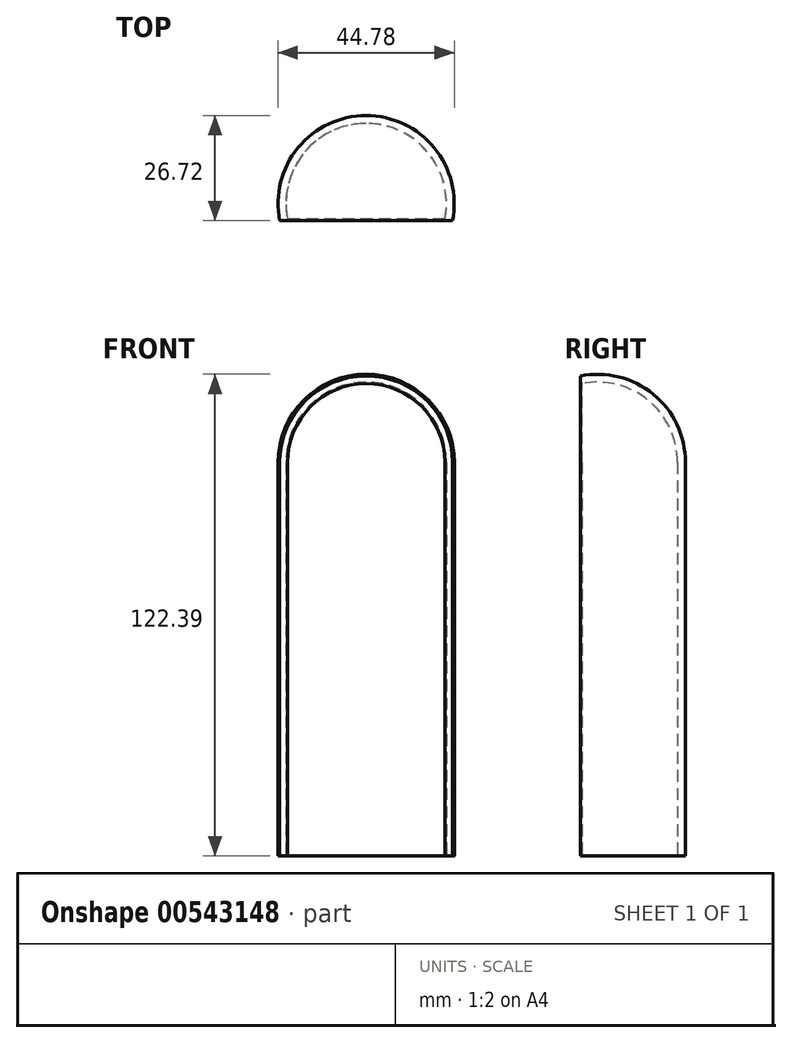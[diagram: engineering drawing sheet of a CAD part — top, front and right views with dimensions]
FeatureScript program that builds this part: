
annotation { "Feature Type Name" : "Feature", "Feature Type Description" : "" }
export const myFeature = defineFeature(function(context is Context, id is Id, definition is map)
    precondition{}
    {
        {
            var Q0;
            Q0=qCreatedBy(makeId("Top.planeOp"),FACE);
            var sketch = newSketch(context, id + "F0", { "sketchPlane" : qUnion([Q0])});
            skArc(sketch, "E0", {"start": v(40, 0) * mm, "mid": v(20, 24.33) * mm, "end": v(0, 0) * mm});
            skArc(sketch, "E1.0", {"start": v(41.96, -0.39) * mm, "mid": v(20, 26.33) * mm, "end": v(-1.96, -0.39) * mm});
            skLineSegment(sketch, "E2", {"start": v(-1.96, -0.39) * mm, "end": v(0, 0) * mm});
            skLineSegment(sketch, "E3", {"start": v(40, 0) * mm, "end": v(41.96, -0.39) * mm});
            skSolve(sketch);
        }
        {
            var Q0;
            Q0=makeQuery(id+"F0.imprint","IMPRINT",FACE,{"disambiguationData":[TD([[makeQuery(id+"F0.imprint","IMPRINT",EDGE,{"derivedFrom":sQuery(id+"F0.wireOp",EDGE,"E0")}),-1.0]])]});
            extrude(context, id + "F1", {"entities" : qUnion([Q0]), "depth" : 100 * mm, "offsetDistance" : 25.4 * mm});
        }
        {
            var Q0;
            Q0=makeQuery(id+"F1.opExtrude","CAP_FACE",FACE,{"disambiguationData":[OSD([sQuery(id+"F0.wireOp",EDGE,"E0"),sQuery(id+"F0.wireOp",EDGE,"E1.0"),sQuery(id+"F0.wireOp",EDGE,"E2"),sQuery(id+"F0.wireOp",EDGE,"E3")])],"isStart":false});
            var sketch = newSketch(context, id + "F2", { "sketchPlane" : qUnion([Q0])});
            skArc(sketch, "E4", {"start": v(20, 24.33) * mm, "mid": v(4.25, 16.89) * mm, "end": v(0, 0) * mm});
            skArc(sketch, "E5.0", {"start": v(20, 26.33) * mm, "mid": v(2.7, 18.16) * mm, "end": v(-1.96, -0.39) * mm});
            skLineSegment(sketch, "E6", {"start": v(-1.96, -0.39) * mm, "end": v(0, 0) * mm});
            skLineSegment(sketch, "E7", {"start": v(20, 0) * mm, "end": v(20, 26.33) * mm});
            skSolve(sketch);
        }
        {
            var Q0;
            {var subQ0=sQuery(id+"F2.wireOp",EDGE,"E4");Q0=makeQuery(id+"F2.imprint","IMPRINT",FACE,{"disambiguationData":[TD([[makeQuery(id+"F2.imprint","IMPRINT",EDGE,{"derivedFrom":subQ0}),-1.0]])]});}
            var Q1;
            Q1=sQuery(id+"F2.wireOp",EDGE,"E7");
            revolve(context, id + "F3", {"operationType" : NewBodyOperationType.ADD, "entities" : qUnion([Q0]), "axis" : qUnion([Q1]), "revolveType" : RevolveType.ONE_DIRECTION, "angle" : 180 * degree});
        }
    });
